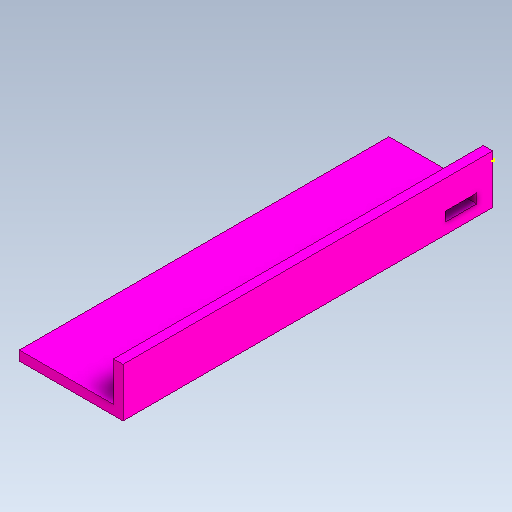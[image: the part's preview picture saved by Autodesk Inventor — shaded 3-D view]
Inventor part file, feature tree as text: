
AUTODESK INVENTOR PART (.ipt)
format: ipt  version: 2020 (Build 240168000, 168)  size: 113,152 bytes
history: native  units: mm
features: sketch x3, other x3, plane x2, extrude x2, reference x1
ambient origin geometry x8: Origin, YZ Plane, XZ Plane, XY Plane, X Axis, Y Axis, Z Axis, Center Point
bodies: Solid1 (feature_tree)
feature tree (11):
  sketch  "Sketch1"  dims[d0=10.0mm d1=0.0mm d2=10.0mm]
  plane  "Work Plane1"
  plane  "Work Plane2"
  extrude  "Extrusion1"  Depth=10.0mm
  sketch  "Sketch2"  dims[d3=3.0mm d4=0.5mm]
  extrude  "Extrusion2"  Depth=0.5mm
  reference  "Reference1"
  sketch  "Sketch3"  dims[d5=5.0mm d6=0.0mm d7=0.0mm]
  parser-record x1  (decoder bookkeeping rows leaked as tree rows — omitted from the tree; the rows remain in map.json)
  other  "steering_queens_pair.iam"
  other  "hull_main:1"
note: 1 file-system path scrubbed to <path> (originals preserved in map.json)
